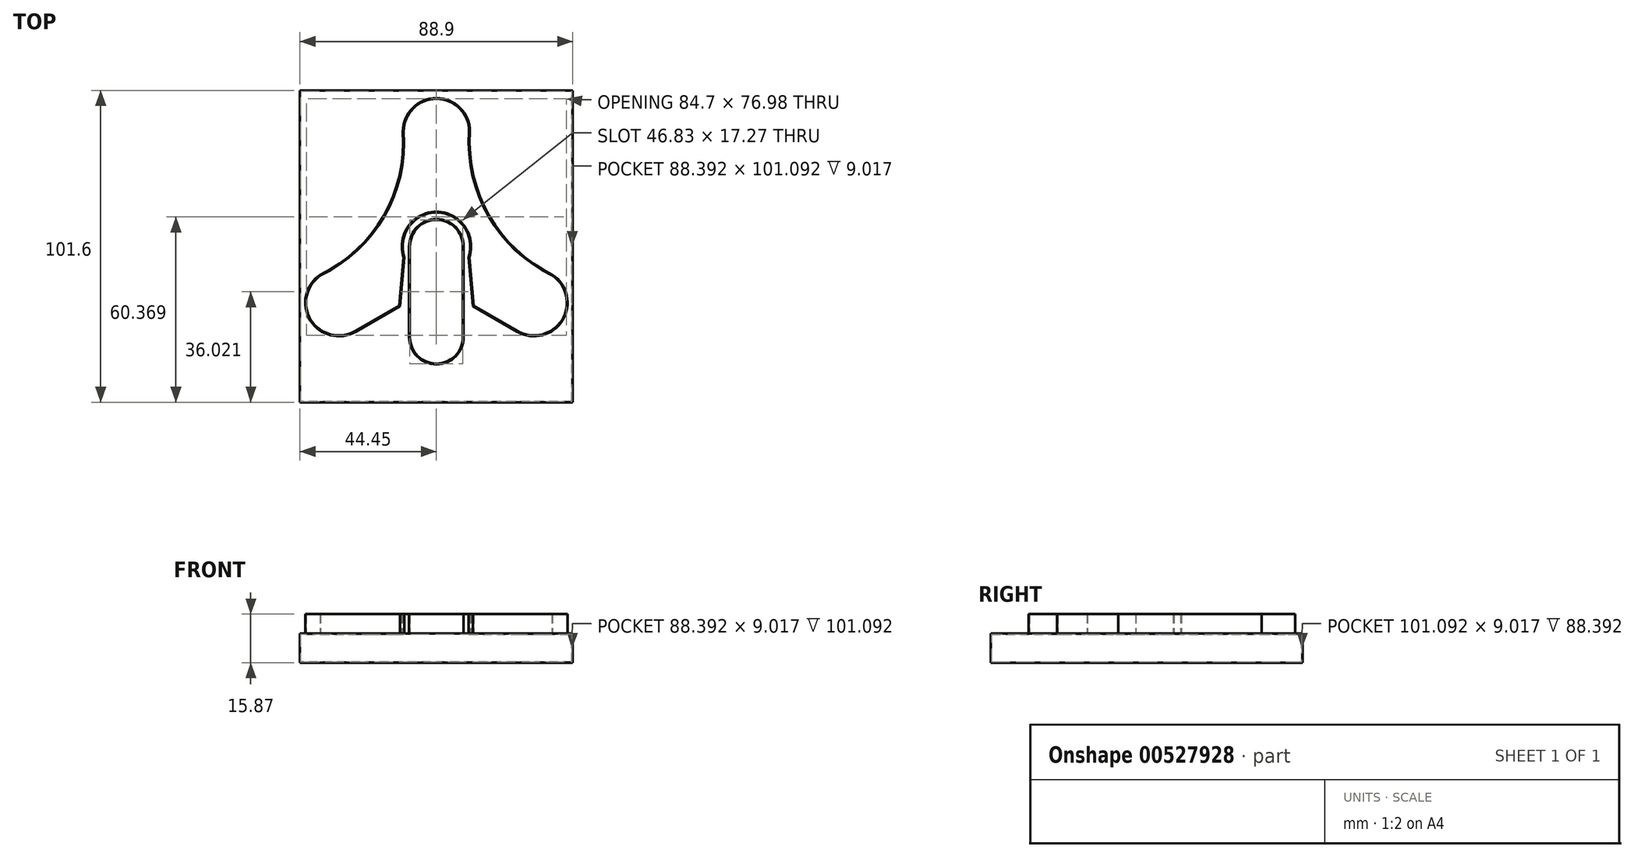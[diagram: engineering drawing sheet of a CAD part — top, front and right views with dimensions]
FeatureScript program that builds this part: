
annotation { "Feature Type Name" : "Feature", "Feature Type Description" : "" }
export const myFeature = defineFeature(function(context is Context, id is Id, definition is map)
    precondition{}
    {
        {
            var Q0;
            Q0=qCreatedBy(makeId("Top.planeOp"),FACE);
            var sketch = newSketch(context, id + "F0", { "sketchPlane" : qUnion([Q0])});
            skArc(sketch, "E0", {"start": v(10.43, -3.55) * mm, "mid": v(0, 11.02) * mm, "end": v(-10.43, -3.55) * mm});
            skLineSegment(sketch, "E1", {"start": v(0, 11.02) * mm, "end": v(0, 37.4) * mm, "construction": true});
            skArc(sketch, "E2", {"start": v(10.84, 36.08) * mm, "mid": v(0, 48.32) * mm, "end": v(-10.84, 36.08) * mm});
            skArc(sketch, "E3.1.0", {"start": v(-35.75, -8.16) * mm, "mid": v(-41.7, -23.07) * mm, "end": v(-26.36, -27.81) * mm});
            skPoint(sketch, "E4.orphan", {"position": v(0, 11.02) * mm});
            skArc(sketch, "E5", {"start": v(8.89, 0) * mm, "mid": v(0, 8.9) * mm, "end": v(-8.9, 0) * mm});
            skArc(sketch, "E6", {"start": v(-8.9, -29.56) * mm, "mid": v(0, -38.45) * mm, "end": v(8.9, -29.56) * mm});
            skLineSegment(sketch, "E7", {"start": v(-8.9, 0) * mm, "end": v(-8.89, -29.56) * mm});
            skLineSegment(sketch, "E8", {"start": v(8.89, 0) * mm, "end": v(8.9, -29.56) * mm});
            skArc(sketch, "E9", {"start": v(-37.84, -9.24) * mm, "mid": v(-17.2, 9.93) * mm, "end": v(-10.92, 37.4) * mm});
            skLineSegment(sketch, "E10", {"start": v(-26.36, -27.81) * mm, "end": v(-11.9, -19.44) * mm});
            skLineSegment(sketch, "E11", {"start": v(-11.9, -19.44) * mm, "end": v(-10.43, -3.55) * mm});
            skPoint(sketch, "E12.endSnap0", {"position": v(10.94, -7.44) * mm});
            skArc(sketch, "E13.MirrorCS", {"start": v(37.84, -9.24) * mm, "mid": v(17.2, 9.93) * mm, "end": v(10.92, 37.4) * mm});
            skArc(sketch, "E14.MirrorC", {"start": v(35.75, -8.16) * mm, "mid": v(41.7, -23.07) * mm, "end": v(26.36, -27.81) * mm});
            skLineSegment(sketch, "E15.MirrorCS", {"start": v(26.36, -27.81) * mm, "end": v(11.9, -19.44) * mm});
            skLineSegment(sketch, "E16.MirrorCS", {"start": v(11.9, -19.44) * mm, "end": v(10.43, -3.55) * mm});
            skSolve(sketch);
        }
        {
            var Q0;
            Q0=makeQuery(id+"F0.imprint","IMPRINT",FACE,{"disambiguationData":[TD([[makeQuery(id+"F0.imprint","IMPRINT",EDGE,{"derivedFrom":sQuery(id+"F0.wireOp",EDGE,"E0")}),-1.0]])]});
            var Q1;
            Q1=makeQuery(id+"F0.imprint","IMPRINT",FACE,{"disambiguationData":[TD([[makeQuery(id+"F0.imprint","IMPRINT",EDGE,{"derivedFrom":sQuery(id+"F0.wireOp",EDGE,"E5")}),1.0]])]});
            extrude(context, id + "F1", {"entities" : qUnion([Q0, Q1]), "depth" : 12.7 * mm, "offsetDistance" : 25.4 * mm});
        }
        {
            var Q0;
            Q0=qCreatedBy(makeId("Top.planeOp"),FACE);
            var sketch = newSketch(context, id + "F2", { "sketchPlane" : qUnion([Q0])});
            skLineSegment(sketch, "E17.bottom", {"start": v(44.45, -50.8) * mm, "end": v(-44.45, -50.8) * mm});
            skLineSegment(sketch, "E17.top", {"start": v(44.45, 50.8) * mm, "end": v(-44.45, 50.8) * mm});
            skLineSegment(sketch, "E17.left", {"start": v(44.45, -50.8) * mm, "end": v(44.45, 50.8) * mm});
            skLineSegment(sketch, "E17.right", {"start": v(-44.45, -50.8) * mm, "end": v(-44.45, 50.8) * mm});
            skPoint(sketch, "E17.middle", {"position": v(0, 0) * mm});
            skSolve(sketch);
        }
        {
            var Q0;
            Q0 = qSketchRegion(id + "F2", true);
            extrude(context, id + "F3", {"entities" : qUnion([Q0]), "endBound" : BoundingType.SYMMETRIC, "oppositeDirection" : true, "depth" : 6.35 * mm, "offsetDistance" : 25.4 * mm});
        }
        {
            var Q0;
            Q0=makeQuery(id+"F3.opExtrude","CAP_FACE",FACE,{"disambiguationData":[OSD([sQuery(id+"F2.wireOp",EDGE,"E17.bottom"),sQuery(id+"F2.wireOp",EDGE,"E17.top"),sQuery(id+"F2.wireOp",EDGE,"E17.left"),sQuery(id+"F2.wireOp",EDGE,"E17.right")])],"isStart":true});
            extrude(context, id + "F4", {"entities" : qUnion([Q0]), "operationType" : NewBodyOperationType.ADD, "depth" : 3.17 * mm, "offsetDistance" : 25.4 * mm});
        }
        {
            var Q0;
            Q0=makeQuery(id+"F1.opExtrude","CAP_FACE",FACE,{"disambiguationData":[OSD([sQuery(id+"F0.wireOp",EDGE,"E0"),sQuery(id+"F0.wireOp",EDGE,"E2"),sQuery(id+"F0.wireOp",EDGE,"E3.1.0"),sQuery(id+"F0.wireOp",EDGE,"E9"),sQuery(id+"F0.wireOp",EDGE,"E10"),sQuery(id+"F0.wireOp",EDGE,"E11"),sQuery(id+"F0.wireOp",EDGE,"E13.MirrorCS"),sQuery(id+"F0.wireOp",EDGE,"E14.MirrorC"),sQuery(id+"F0.wireOp",EDGE,"E15.MirrorCS"),sQuery(id+"F0.wireOp",EDGE,"E16.MirrorCS")])],"isStart":false});
            var Q1;
            Q1=makeQuery(id+"F1.opExtrude","CAP_FACE",FACE,{"disambiguationData":[OSD([sQuery(id+"F0.wireOp",EDGE,"E5"),sQuery(id+"F0.wireOp",EDGE,"E6"),sQuery(id+"F0.wireOp",EDGE,"E7"),sQuery(id+"F0.wireOp",EDGE,"E8")])],"isStart":false});
            shell(context, id + "F5", {"entities" : qUnion([Q0, Q1]), "thickness" : 0.25 * mm});
        }
    });
